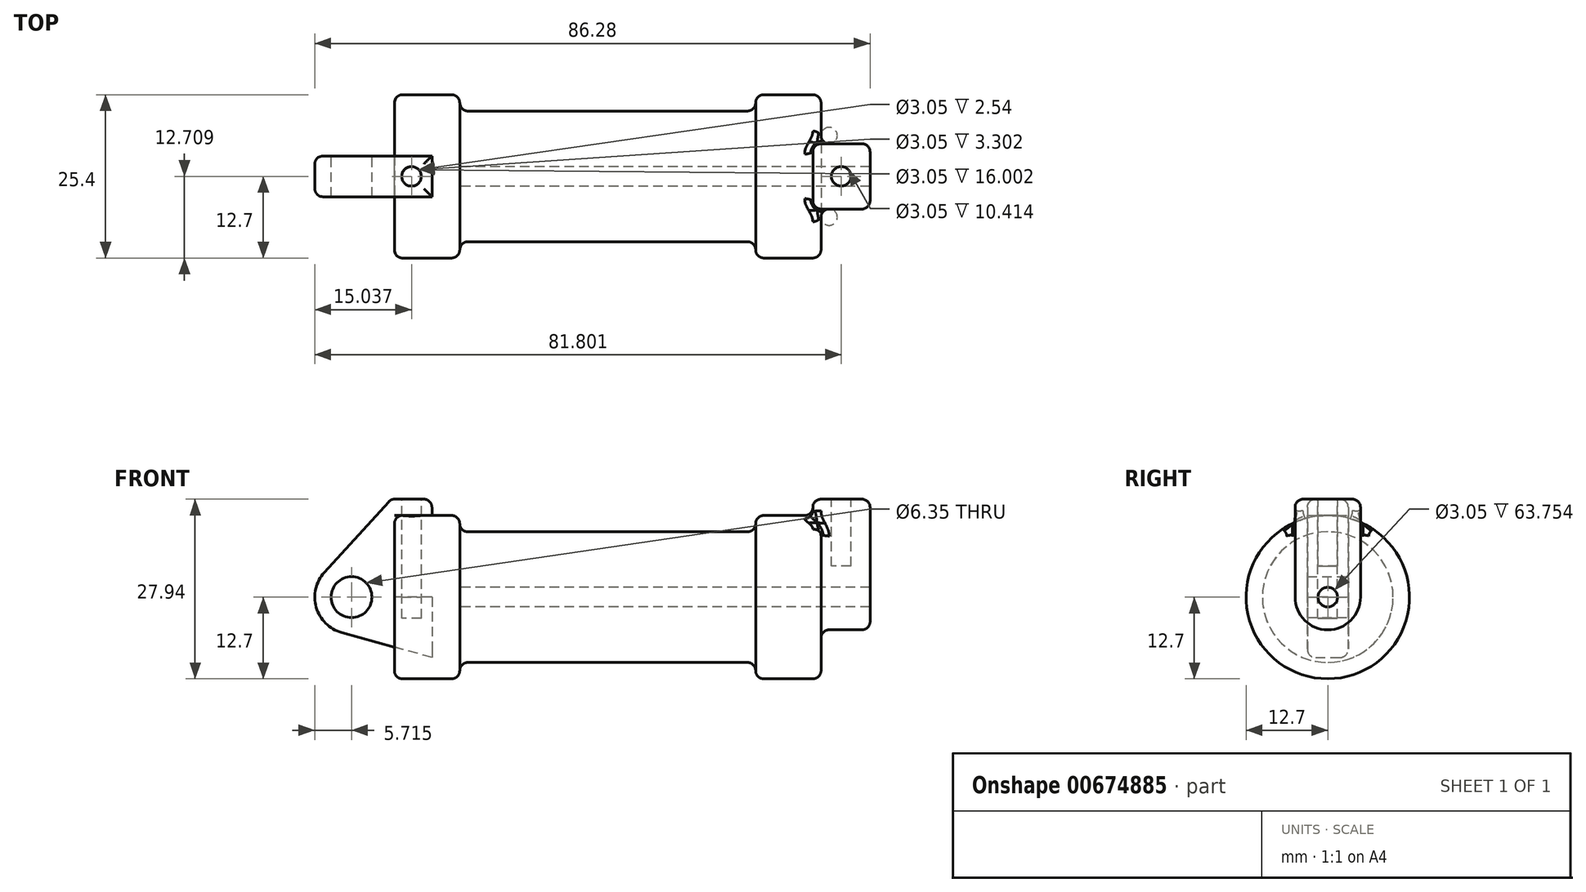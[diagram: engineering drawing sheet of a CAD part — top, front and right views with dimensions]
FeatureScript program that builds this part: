
annotation { "Feature Type Name" : "Feature", "Feature Type Description" : "" }
export const myFeature = defineFeature(function(context is Context, id is Id, definition is map)
    precondition{}
    {
        {
            var Q0;
            Q0=qCreatedBy(makeId("Front.planeOp"),FACE);
            var sketch = newSketch(context, id + "F0", { "sketchPlane" : qUnion([Q0])});
            skLineSegment(sketch, "E0", {"start": v(0, 0) * mm, "end": v(0, 12.7) * mm});
            skLineSegment(sketch, "E1", {"start": v(0, 12.7) * mm, "end": v(10.16, 12.7) * mm});
            skLineSegment(sketch, "E2", {"start": v(10.16, 12.7) * mm, "end": v(10.16, 10.16) * mm});
            skLineSegment(sketch, "E3", {"start": v(10.16, 10.16) * mm, "end": v(56.13, 10.16) * mm});
            skLineSegment(sketch, "E4", {"start": v(56.13, 10.16) * mm, "end": v(56.13, 12.7) * mm});
            skLineSegment(sketch, "E5", {"start": v(56.13, 12.7) * mm, "end": v(66.3, 12.7) * mm});
            skLineSegment(sketch, "E6", {"start": v(66.3, 12.7) * mm, "end": v(66.3, 0) * mm});
            skLineSegment(sketch, "E7", {"start": v(66.3, 0) * mm, "end": v(0, 0) * mm});
            skLineSegment(sketch, "E8", {"start": v(5.84, 15.24) * mm, "end": v(-0.5, 15.24) * mm});
            skLineSegment(sketch, "E9", {"start": v(-0.5, 15.24) * mm, "end": v(-10.88, 3.85) * mm});
            skLineSegment(sketch, "E10", {"start": v(0, 0) * mm, "end": v(-6.65, 0) * mm});
            skCircle(sketch, "E11", {"center": v(-6.65, 0) * mm, "radius": 5.72 * mm});
            skCircle(sketch, "E12", {"center": v(-6.65, 0) * mm, "radius": 3.18 * mm});
            skLineSegment(sketch, "E13", {"start": v(5.84, 15.24) * mm, "end": v(5.84, -9.4) * mm});
            skLineSegment(sketch, "E14", {"start": v(5.84, -9.4) * mm, "end": v(-8.18, -5.5) * mm});
            skSolve(sketch);
        }
        {
            var Q0;
            {var subQ0=sQuery(id+"F0.wireOp",EDGE,"E2");Q0=makeQuery(id+"F0.imprint","IMPRINT",FACE,{"disambiguationData":[TD([[makeQuery(id+"F0.imprint","IMPRINT",EDGE,{"derivedFrom":subQ0}),-1.0]])]});}
            var Q1;
            {var subQ0=sQuery(id+"F0.wireOp",EDGE,"E0");Q1=makeQuery(id+"F0.imprint","IMPRINT",FACE,{"disambiguationData":[TD([[makeQuery(id+"F0.imprint","IMPRINT",EDGE,{"derivedFrom":subQ0}),-1.0]])]});}
            var Q2;
            Q2=sQuery(id+"F0.wireOp",EDGE,"E7");
            revolve(context, id + "F1", {"entities" : qUnion([Q0, Q1]), "axis" : qUnion([Q2]), "revolveType" : RevolveType.FULL});
        }
        {
            var Q0;
            {var subQ1=sQuery(id+"F0.wireOp",EDGE,"E0");Q0=makeQuery(id+"F0.imprint","IMPRINT",FACE,{"disambiguationData":[TD([[makeQuery(id+"F0.imprint","IMPRINT",EDGE,{"derivedFrom":subQ1}),1.0]])]});}
            var Q1;
            {var subQ0=sQuery(id+"F0.wireOp",EDGE,"E14");Q1=makeQuery(id+"F0.imprint","IMPRINT",FACE,{"disambiguationData":[TD([[makeQuery(id+"F0.imprint","IMPRINT",EDGE,{"derivedFrom":subQ0}),-1.0]])]});}
            var Q2;
            {var subQ5=sQuery(id+"F0.wireOp",EDGE,"E12");Q2=makeQuery(id+"F0.imprint","IMPRINT",FACE,{"disambiguationData":[TD([[makeQuery(id+"F0.imprint","IMPRINT",EDGE,{"derivedFrom":subQ5}),-1.0]])]});}
            extrude(context, id + "F2", {"entities" : qUnion([Q0, Q1, Q2]), "endBound" : BoundingType.SYMMETRIC, "depth" : 6.35 * mm, "offsetDistance" : 25.4 * mm});
        }
        {
            var Q0;
            Q0=makeQuery(id+"F1.opRevolve","SWEPT_FACE",FACE,{"disambiguationData":[OSD([sQuery(id+"F0.wireOp",EDGE,"E6")])]});
            var sketch = newSketch(context, id + "F3", { "sketchPlane" : qUnion([Q0])});
            skCircle(sketch, "E15", {"center": v(0, 0) * mm, "radius": 1.52 * mm});
            skCircle(sketch, "E16", {"center": v(0, 0) * mm, "radius": 5.08 * mm});
            skLineSegment(sketch, "E17", {"start": v(-5.08, 15.24) * mm, "end": v(5.08, 15.24) * mm});
            skLineSegment(sketch, "E18", {"start": v(-5.08, 15.24) * mm, "end": v(-5.08, 0) * mm});
            skLineSegment(sketch, "E19", {"start": v(5.08, 15.24) * mm, "end": v(5.08, 0) * mm});
            skSolve(sketch);
        }
        {
            var Q0;
            Q0 = qSketchRegion(id + "F3", true);
            extrude(context, id + "F4", {"entities" : qUnion([Q0]), "operationType" : NewBodyOperationType.ADD, "depth" : 7.62 * mm, "offsetDistance" : 25.4 * mm});
        }
        {
            var Q0;
            Q0 = qSketchRegion(id + "F3", true);
            extrude(context, id + "F5", {"entities" : qUnion([Q0]), "operationType" : NewBodyOperationType.ADD, "oppositeDirection" : true, "depth" : 1.27 * mm, "offsetDistance" : 25.4 * mm});
        }
        {
            var Q0;
            Q0=makeQuery(id+"F3.imprint","IMPRINT",FACE,{"disambiguationData":[TD([[makeQuery(id+"F3.imprint","IMPRINT",EDGE,{"derivedFrom":sQuery(id+"F3.wireOp",EDGE,"E15")}),1.0]])]});
            var Q1;
            Q1=makeQuery(id+"F1.opRevolve","SWEPT_FACE",FACE,{"disambiguationData":[OSD([sQuery(id+"F0.wireOp",EDGE,"E2")])]});
            extrude(context, id + "F6", {"entities" : qUnion([Q0]), "operationType" : NewBodyOperationType.ADD, "endBound" : BoundingType.UP_TO_SURFACE, "oppositeDirection" : true, "depth" : 57.4 * mm, "endBoundEntityFace" : qUnion([Q1]), "offsetDistance" : 25.4 * mm});
        }
        {
            var Q0;
            Q0=makeQuery(id+"F4.boolean.opBoolean","SPLIT",FACE,{"disambiguationData":[TD([makeQuery(id+"F4.opExtrude","SWEPT_FACE",FACE,{"disambiguationData":[OSD([sQuery(id+"F3.wireOp",EDGE,"E15")])]})])],"derivedFrom":makeQuery(id+"F1.opRevolve","SWEPT_FACE",FACE,{"disambiguationData":[OSD([sQuery(id+"F0.wireOp",EDGE,"E6")])]})});
            var Q1;
            Q1=makeQuery(id+"F1.opRevolve","SWEPT_FACE",FACE,{"disambiguationData":[OSD([sQuery(id+"F0.wireOp",EDGE,"E2")])]});
            extrude(context, id + "F7", {"entities" : qUnion([Q0]), "operationType" : NewBodyOperationType.REMOVE, "endBound" : BoundingType.UP_TO_SURFACE, "oppositeDirection" : true, "depth" : 25.4 * mm, "endBoundEntityFace" : qUnion([Q1]), "offsetDistance" : 25.4 * mm});
        }
        {
            var Q0;
            Q0=makeQuery(id+"F2.opExtrude","SWEPT_FACE",FACE,{"disambiguationData":[OSD([sQuery(id+"F0.wireOp",EDGE,"E8")])]});
            var sketch = newSketch(context, id + "F8", { "sketchPlane" : qUnion([Q0])});
            skCircle(sketch, "E20", {"center": v(2.67, 0) * mm, "radius": 1.52 * mm});
            skSolve(sketch);
        }
        {
            var Q0;
            Q0=makeQuery(id+"F8.imprint","IMPRINT",FACE,{"disambiguationData":[TD([[makeQuery(id+"F8.imprint","IMPRINT",EDGE,{"derivedFrom":sQuery(id+"F8.wireOp",EDGE,"E20")}),1.0]])]});
            extrude(context, id + "F9", {"entities" : qUnion([Q0]), "operationType" : NewBodyOperationType.REMOVE, "oppositeDirection" : true, "depth" : 18.54 * mm, "offsetDistance" : 25.4 * mm});
        }
        {
            var Q0;
            {var subQ0=sQuery(id+"F3.wireOp",EDGE,"E17");Q0=makeQuery(id+"F5.boolean.opBoolean","MERGE",FACE,{"derivedFrom":[makeQuery(id+"F4.opExtrude","SWEPT_FACE",FACE,{"disambiguationData":[OSD([subQ0])]}),makeQuery(id+"F5.opExtrude","SWEPT_FACE",FACE,{"disambiguationData":[OSD([subQ0])]})]});}
            var sketch = newSketch(context, id + "F10", { "sketchPlane" : qUnion([Q0])});
            skCircle(sketch, "E21", {"center": v(69.43, 0) * mm, "radius": 1.52 * mm});
            skSolve(sketch);
        }
        {
            var Q0;
            Q0=makeQuery(id+"F10.imprint","IMPRINT",FACE,{"disambiguationData":[TD([[makeQuery(id+"F10.imprint","IMPRINT",EDGE,{"derivedFrom":sQuery(id+"F10.wireOp",EDGE,"E21")}),1.0]])]});
            extrude(context, id + "F11", {"entities" : qUnion([Q0]), "operationType" : NewBodyOperationType.REMOVE, "oppositeDirection" : true, "depth" : 10.4 * mm, "offsetDistance" : 25.4 * mm});
        }
        {
            var Q0;
            Q0=makeQuery(id+"F1.opRevolve","SWEPT_FACE",FACE,{"disambiguationData":[OSD([sQuery(id+"F0.wireOp",EDGE,"E2")])]});
            var Q1;
            Q1=makeQuery(id+"F1.opRevolve","SWEPT_FACE",FACE,{"disambiguationData":[OSD([sQuery(id+"F0.wireOp",EDGE,"E3")])]});
            fillet(context, id + "F12", {"entities" : qUnion([Q0, Q1]), "radius" : 1.27 * mm, "tangentPropagation" : true, "allowEdgeOverflow" : false});
        }
        {
            var Q0;
            Q0=makeQuery(id+"F1.opRevolve","SWEPT_FACE",FACE,{"disambiguationData":[OSD([sQuery(id+"F0.wireOp",EDGE,"E4")])]});
            fillet(context, id + "F13", {"entities" : qUnion([Q0]), "radius" : 1.27 * mm, "tangentPropagation" : true, "allowEdgeOverflow" : false});
        }
        {
            var Q0;
            Q0=makeQuery(id+"F1.opRevolve","SWEPT_FACE",FACE,{"disambiguationData":[OSD([sQuery(id+"F0.wireOp",EDGE,"E5")])]});
            var Q1;
            Q1=makeQuery(id+"F4.boolean.opBoolean","SPLIT",FACE,{"disambiguationData":[TD([makeQuery(id+"F1.opRevolve","SWEPT_FACE",FACE,{"disambiguationData":[OSD([sQuery(id+"F0.wireOp",EDGE,"E5")])]})])],"derivedFrom":makeQuery(id+"F1.opRevolve","SWEPT_FACE",FACE,{"disambiguationData":[OSD([sQuery(id+"F0.wireOp",EDGE,"E6")])]})});
            var Q2;
            Q2=makeQuery(id+"F4.opExtrude","SWEPT_FACE",FACE,{"disambiguationData":[OSD([sQuery(id+"F3.wireOp",EDGE,"E16")])]});
            var Q3;
            {var subQ0=sQuery(id+"F3.wireOp",EDGE,"E19");Q3=makeQuery(id+"F5.boolean.opBoolean","MERGE",FACE,{"derivedFrom":[makeQuery(id+"F4.opExtrude","SWEPT_FACE",FACE,{"disambiguationData":[OSD([subQ0])]}),makeQuery(id+"F5.opExtrude","SWEPT_FACE",FACE,{"disambiguationData":[OSD([subQ0])]})]});}
            var Q4;
            {var subQ0=sQuery(id+"F3.wireOp",EDGE,"E18");Q4=makeQuery(id+"F5.boolean.opBoolean","MERGE",FACE,{"derivedFrom":[makeQuery(id+"F4.opExtrude","SWEPT_FACE",FACE,{"disambiguationData":[OSD([subQ0])]}),makeQuery(id+"F5.opExtrude","SWEPT_FACE",FACE,{"disambiguationData":[OSD([subQ0])]})]});}
            fillet(context, id + "F14", {"entities" : qUnion([Q0, Q1, Q2, Q3, Q4]), "radius" : 1.27 * mm, "tangentPropagation" : true, "allowEdgeOverflow" : false});
        }
        {
            var Q0;
            Q0=makeQuery(id+"F4.opExtrude","CAP_EDGE",EDGE,{"disambiguationData":[OSD([sQuery(id+"F3.wireOp",EDGE,"E17")])],"isStart":false});
            var Q1;
            Q1=makeQuery(id+"F5.opExtrude","CAP_EDGE",EDGE,{"disambiguationData":[OSD([sQuery(id+"F3.wireOp",EDGE,"E17")])],"isStart":false});
            fillet(context, id + "F15", {"entities" : qUnion([Q0, Q1]), "radius" : 1.27 * mm, "tangentPropagation" : true, "allowEdgeOverflow" : false});
        }
        {
            var Q0;
            Q0=makeQuery(id+"F1.opRevolve","SWEPT_EDGE",EDGE,{"disambiguationData":[OSD([sQuery(id+"F0.wireOp",EDGE,"E0"),sQuery(id+"F0.wireOp",EDGE,"E1")])]});
            var Q1;
            Q1=makeQuery(id+"F2.opExtrude","CAP_EDGE",EDGE,{"disambiguationData":[OSD([sQuery(id+"F0.wireOp",EDGE,"E9")])],"isStart":true});
            var Q2;
            Q2=makeQuery(id+"F2.opExtrude","CAP_EDGE",EDGE,{"disambiguationData":[OSD([sQuery(id+"F0.wireOp",EDGE,"E9")])],"isStart":false});
            var Q3;
            Q3=makeQuery(id+"F2.opExtrude","SWEPT_EDGE",EDGE,{"disambiguationData":[OSD([sQuery(id+"F0.wireOp",EDGE,"E8"),sQuery(id+"F0.wireOp",EDGE,"E9")])]});
            var Q4;
            Q4=makeQuery(id+"F2.opExtrude","CAP_EDGE",EDGE,{"disambiguationData":[OSD([sQuery(id+"F0.wireOp",EDGE,"E8")])],"isStart":true});
            var Q5;
            Q5=makeQuery(id+"F2.opExtrude","SWEPT_EDGE",EDGE,{"disambiguationData":[OSD([sQuery(id+"F0.wireOp",EDGE,"E8"),sQuery(id+"F0.wireOp",EDGE,"E13")])]});
            var Q6;
            Q6=makeQuery(id+"F2.opExtrude","CAP_EDGE",EDGE,{"disambiguationData":[OSD([sQuery(id+"F0.wireOp",EDGE,"E8")])],"isStart":false});
            fillet(context, id + "F16", {"entities" : qUnion([Q0, Q1, Q2, Q3, Q4, Q5, Q6]), "radius" : 1.27 * mm, "tangentPropagation" : true, "allowEdgeOverflow" : false});
        }
    });
